# Revit family: HL_Душевой трап_HL570
name_source: partatom
category: Instalační zařizovací předměty
revit_build: Autodesk Revit 2016 (Build: 20151007_0715(x64)
units: mm (PartAtom-declared; Revit-internal decimal feet)

## family parameters
Bod výpočtu místnosti = Ano
Kóta kulaté spojky = Použít průměr
Nadpis OmniClass = Deck Waste Water Drains
Ořezat dutým tvarem při načtení = Ne
Sdílené = Ne
Typ součásti = Normální
Vždy vertikální = Ano
Založené na pracovní rovině = Ne
Číslo OmniClass = 23.70.50.21.24.14

## types (1)
- HL_Душевой трап_HL570
    EAN = 9003076049998
    Klíčová poznámka = HL570
    Komentáře k typům = HL570 FlexBox
    Model = HL570
    Popis = Душевой трап
    Připojení CW = Ne
    Připojení HW = Ne
    Připojení odpadu = Ano
    Připojení ventilace = Ne
    URL = http://www.hutterer-lechner.com
    Výrobce = HL Hutterer & Lechner GmbH
    ВЕС = 0,53 [kg]
    ВЫСОТА МОНТАЖА = (80) 100 - 200mm (250mm)
    МАКСИМАЛЬНАЯ НАГРУЗКА КЛАССА = K3 - 300kg
    МАТЕРИАЛ = PP/TPE/Edelstahl
    НОРМЫ = EN274
    ПРОИЗВОДИТЕЛЬНОСТЬ = 0,50 l/s
    РАЗМЕР = DN40/50
    РЕШЁТКА = Edelstahl

## geometry (parser evidence)
native form markers: Sweep x8
no freeform markers — native parametric forms only
